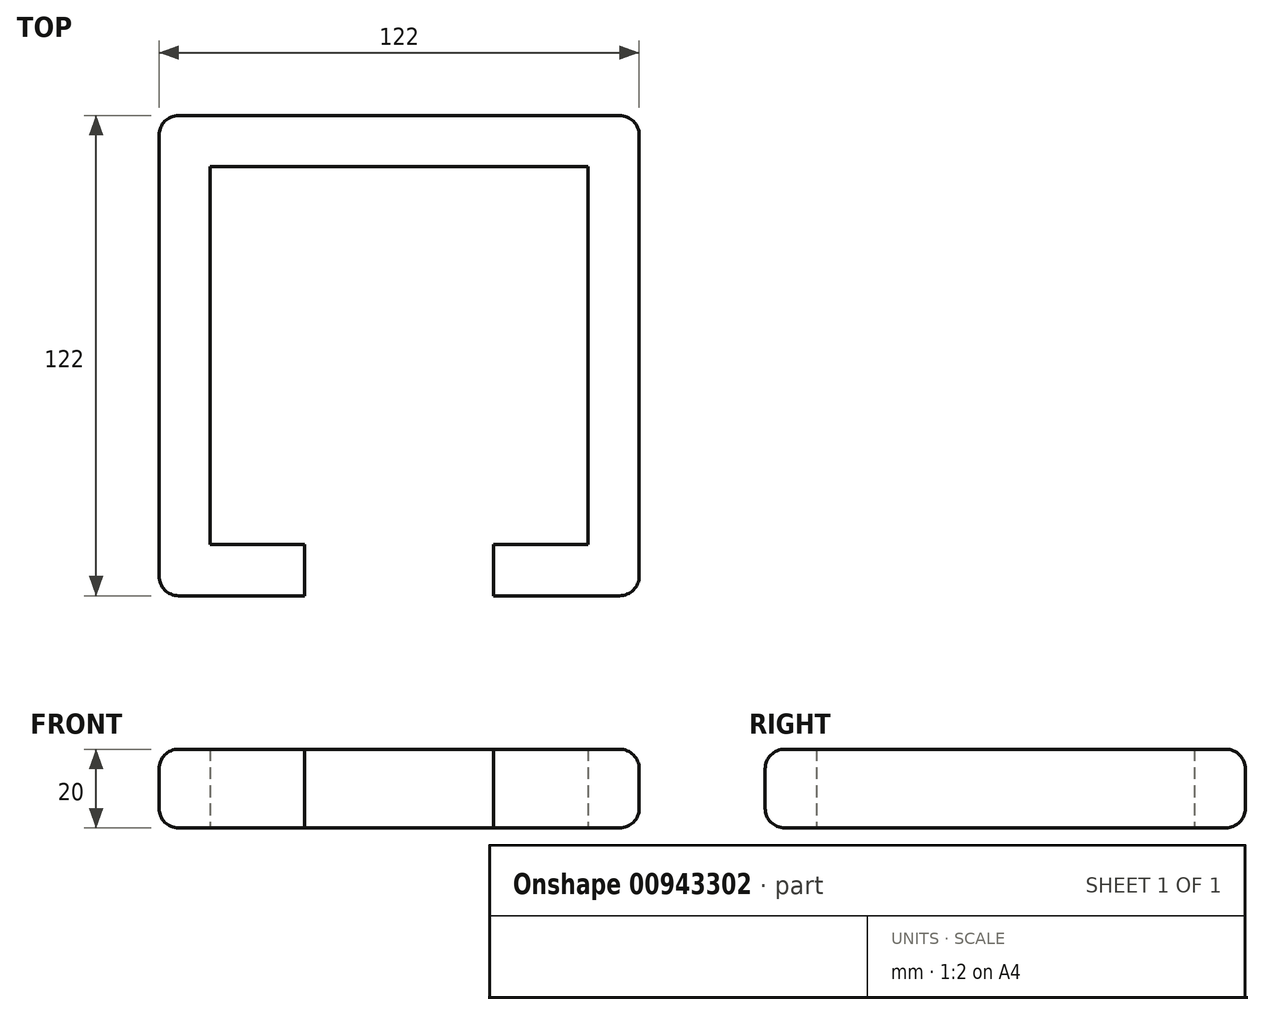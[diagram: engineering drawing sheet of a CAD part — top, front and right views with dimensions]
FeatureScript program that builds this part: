
annotation { "Feature Type Name" : "Feature", "Feature Type Description" : "" }
export const myFeature = defineFeature(function(context is Context, id is Id, definition is map)
    precondition{}
    {
        {
            var Q0;
            Q0=qCreatedBy(makeId("Top.planeOp"),FACE);
            var sketch = newSketch(context, id + "F0", { "sketchPlane" : qUnion([Q0])});
            skLineSegment(sketch, "E0.bottom", {"start": v(61, 61) * mm, "end": v(-61, 61) * mm});
            skLineSegment(sketch, "E0.top", {"start": v(61, -61) * mm, "end": v(-61, -61) * mm});
            skLineSegment(sketch, "E0.left", {"start": v(61, 61) * mm, "end": v(61, -61) * mm});
            skLineSegment(sketch, "E0.right", {"start": v(-61, 61) * mm, "end": v(-61, -61) * mm});
            skPoint(sketch, "E0.middle", {"position": v(0, 0) * mm});
            skLineSegment(sketch, "E1.bottom", {"start": v(48, 48) * mm, "end": v(-48, 48) * mm});
            skLineSegment(sketch, "E1.top", {"start": v(48, -48) * mm, "end": v(-48, -48) * mm});
            skLineSegment(sketch, "E1.left", {"start": v(48, 48) * mm, "end": v(48, -48) * mm});
            skLineSegment(sketch, "E1.right", {"start": v(-48, 48) * mm, "end": v(-48, -48) * mm});
            skLineSegment(sketch, "E2", {"start": v(-24, -48) * mm, "end": v(-24, -61) * mm});
            skLineSegment(sketch, "E3", {"start": v(24, -48) * mm, "end": v(24, -61) * mm});
            skSolve(sketch);
        }
        {
            var Q0;
            Q0=makeQuery(id+"F0.imprint","IMPRINT",FACE,{"disambiguationData":[TD([[makeQuery(id+"F0.imprint","IMPRINT",EDGE,{"derivedFrom":sQuery(id+"F0.wireOp",EDGE,"E0.bottom")}),1.0]])]});
            extrude(context, id + "F1", {"entities" : qUnion([Q0]), "depth" : 20 * mm, "offsetDistance" : 25 * mm});
        }
        {
            var Q0;
            Q0=makeQuery(id+"F1.opExtrude","CAP_EDGE",EDGE,{"disambiguationData":[OSD([sQuery(id+"F0.wireOp",EDGE,"E0.right")])],"isStart":false});
            var Q1;
            {var subQ0=sQuery(id+"F0.wireOp",EDGE,"E0.top");Q1=makeQuery(id+"F1.opExtrude","CAP_EDGE",EDGE,{"disambiguationData":[OSD([subQ0]),TDD([makeQuery(id+"F0.imprint","IMPRINT",EDGE,{"disambiguationData":[TD([[makeQuery(id+"F0.imprint","INTERSECT",VERTEX,{"derivedFrom":[subQ0,sQuery(id+"F0.wireOp",EDGE,"E0.right")]}),1.0]])],"derivedFrom":subQ0})])],"isStart":false});}
            var Q2;
            {var subQ0=sQuery(id+"F0.wireOp",EDGE,"E0.top");Q2=makeQuery(id+"F1.opExtrude","CAP_EDGE",EDGE,{"disambiguationData":[OSD([subQ0]),TDD([makeQuery(id+"F0.imprint","IMPRINT",EDGE,{"disambiguationData":[TD([[makeQuery(id+"F0.imprint","INTERSECT",VERTEX,{"derivedFrom":[subQ0,sQuery(id+"F0.wireOp",EDGE,"E0.left")]}),-1.0]])],"derivedFrom":subQ0})])],"isStart":false});}
            var Q3;
            Q3=makeQuery(id+"F1.opExtrude","CAP_EDGE",EDGE,{"disambiguationData":[OSD([sQuery(id+"F0.wireOp",EDGE,"E0.left")])],"isStart":false});
            var Q4;
            Q4=makeQuery(id+"F1.opExtrude","CAP_EDGE",EDGE,{"disambiguationData":[OSD([sQuery(id+"F0.wireOp",EDGE,"E0.bottom")])],"isStart":false});
            var Q5;
            {var subQ0=sQuery(id+"F0.wireOp",EDGE,"E0.top");Q5=makeQuery(id+"F1.opExtrude","CAP_EDGE",EDGE,{"disambiguationData":[OSD([subQ0]),TDD([makeQuery(id+"F0.imprint","IMPRINT",EDGE,{"disambiguationData":[TD([[makeQuery(id+"F0.imprint","INTERSECT",VERTEX,{"derivedFrom":[subQ0,sQuery(id+"F0.wireOp",EDGE,"E0.left")]}),-1.0]])],"derivedFrom":subQ0})])],"isStart":true});}
            var Q6;
            {var subQ0=sQuery(id+"F0.wireOp",EDGE,"E0.top");Q6=makeQuery(id+"F1.opExtrude","CAP_EDGE",EDGE,{"disambiguationData":[OSD([subQ0]),TDD([makeQuery(id+"F0.imprint","IMPRINT",EDGE,{"disambiguationData":[TD([[makeQuery(id+"F0.imprint","INTERSECT",VERTEX,{"derivedFrom":[subQ0,sQuery(id+"F0.wireOp",EDGE,"E0.right")]}),1.0]])],"derivedFrom":subQ0})])],"isStart":true});}
            var Q7;
            Q7=makeQuery(id+"F1.opExtrude","CAP_EDGE",EDGE,{"disambiguationData":[OSD([sQuery(id+"F0.wireOp",EDGE,"E0.right")])],"isStart":true});
            var Q8;
            Q8=makeQuery(id+"F1.opExtrude","CAP_EDGE",EDGE,{"disambiguationData":[OSD([sQuery(id+"F0.wireOp",EDGE,"E0.bottom")])],"isStart":true});
            var Q9;
            Q9=makeQuery(id+"F1.opExtrude","CAP_EDGE",EDGE,{"disambiguationData":[OSD([sQuery(id+"F0.wireOp",EDGE,"E0.left")])],"isStart":true});
            var Q10;
            Q10=makeQuery(id+"F1.opExtrude","SWEPT_EDGE",EDGE,{"disambiguationData":[OSD([sQuery(id+"F0.wireOp",EDGE,"E0.top"),sQuery(id+"F0.wireOp",EDGE,"E0.left")])]});
            var Q11;
            Q11=makeQuery(id+"F1.opExtrude","SWEPT_EDGE",EDGE,{"disambiguationData":[OSD([sQuery(id+"F0.wireOp",EDGE,"E0.top"),sQuery(id+"F0.wireOp",EDGE,"E0.right")])]});
            var Q12;
            Q12=makeQuery(id+"F1.opExtrude","SWEPT_EDGE",EDGE,{"disambiguationData":[OSD([sQuery(id+"F0.wireOp",EDGE,"E0.bottom"),sQuery(id+"F0.wireOp",EDGE,"E0.left")])]});
            var Q13;
            Q13=makeQuery(id+"F1.opExtrude","SWEPT_EDGE",EDGE,{"disambiguationData":[OSD([sQuery(id+"F0.wireOp",EDGE,"E0.bottom"),sQuery(id+"F0.wireOp",EDGE,"E0.right")])]});
            fillet(context, id + "F2", {"entities" : qUnion([Q0, Q1, Q2, Q3, Q4, Q5, Q6, Q7, Q8, Q9, Q10, Q11, Q12, Q13]), "radius" : 5 * mm, "tangentPropagation" : true, "allowEdgeOverflow" : false});
        }
    });
